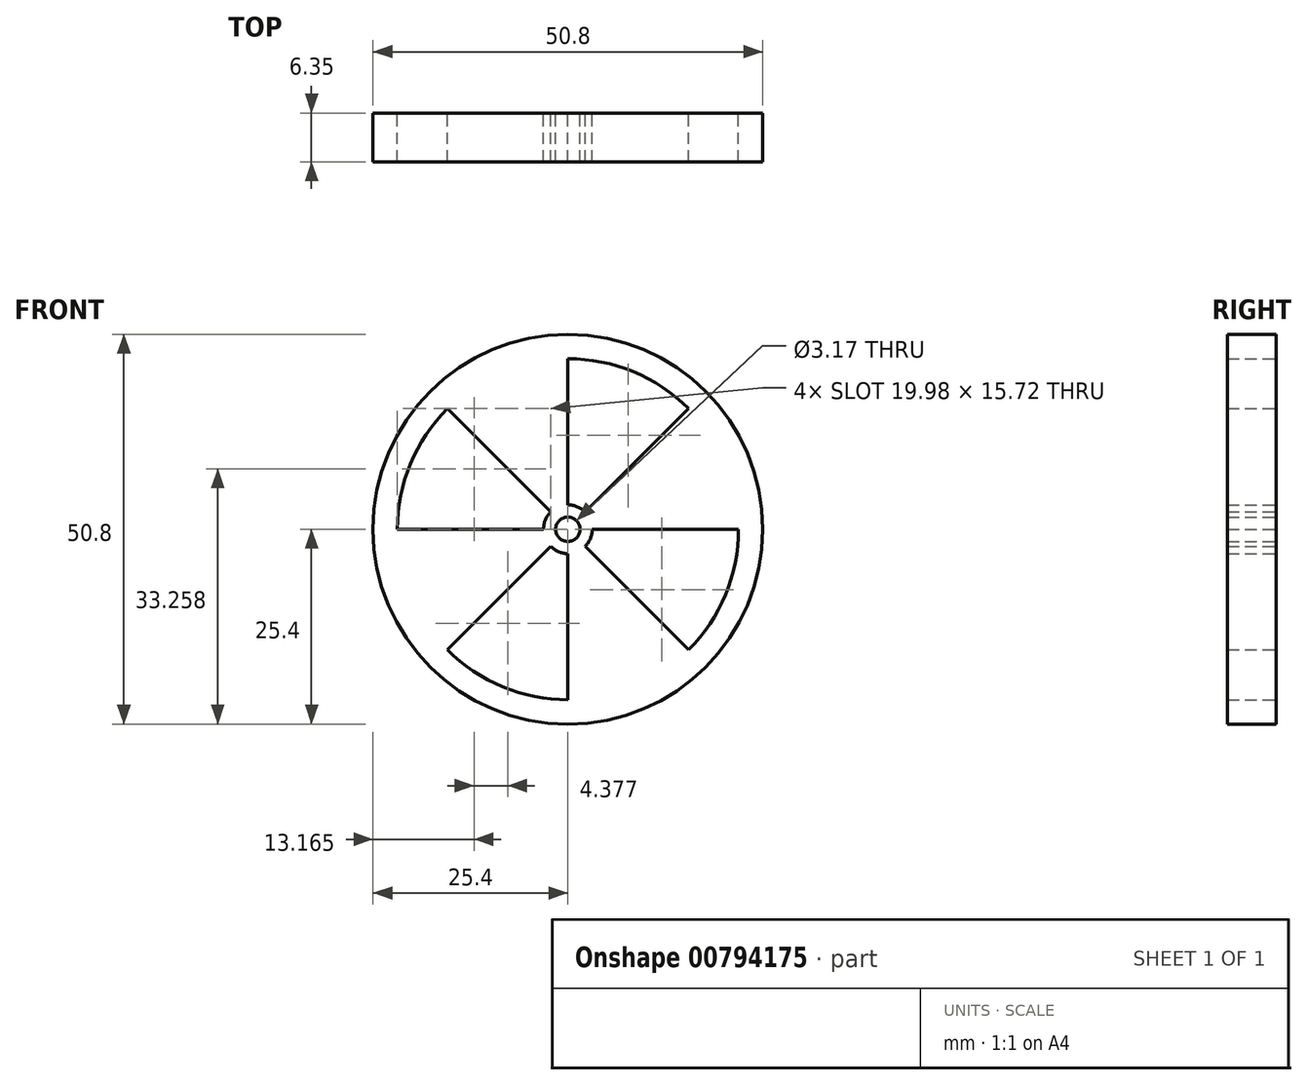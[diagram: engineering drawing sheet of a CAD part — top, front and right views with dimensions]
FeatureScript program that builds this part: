
annotation { "Feature Type Name" : "Feature", "Feature Type Description" : "" }
export const myFeature = defineFeature(function(context is Context, id is Id, definition is map)
    precondition{}
    {
        {
            var Q0;
            Q0=qCreatedBy(makeId("Front.planeOp"),FACE);
            var sketch = newSketch(context, id + "F0", { "sketchPlane" : qUnion([Q0])});
            skCircle(sketch, "E0", {"center": v(0, 0) * mm, "radius": 1.59 * mm});
            skCircle(sketch, "E1", {"center": v(0, 0) * mm, "radius": 3.18 * mm});
            skCircle(sketch, "E2", {"center": v(0, 0) * mm, "radius": 22.23 * mm});
            skCircle(sketch, "E3", {"center": v(0, 0) * mm, "radius": 25.4 * mm});
            skLineSegment(sketch, "E4", {"start": v(0, 3.18) * mm, "end": v(0, 22.23) * mm});
            skLineSegment(sketch, "E5.1.0", {"start": v(-3.18, 0) * mm, "end": v(-22.23, 0) * mm});
            skLineSegment(sketch, "E5.2.0", {"start": v(0, -3.18) * mm, "end": v(0, -22.23) * mm});
            skLineSegment(sketch, "E5.3.0", {"start": v(3.18, 0) * mm, "end": v(22.23, 0) * mm});
            skLineSegment(sketch, "E5.3.1", {"start": v(2.25, -2.25) * mm, "end": v(15.72, -15.72) * mm});
            skLineSegment(sketch, "E6.trimOffspring", {"start": v(-2.25, 2.25) * mm, "end": v(-15.72, 15.72) * mm});
            skLineSegment(sketch, "E7.trimOffspring", {"start": v(2.25, 2.25) * mm, "end": v(15.72, 15.72) * mm});
            skLineSegment(sketch, "E8.trimOffspring", {"start": v(-2.25, -2.25) * mm, "end": v(-15.72, -15.72) * mm});
            skSolve(sketch);
        }
        {
            var Q0;
            {var subQ0=sQuery(id+"F0.wireOp",EDGE,"E4");Q0=makeQuery(id+"F0.imprint","IMPRINT",FACE,{"disambiguationData":[TD([[makeQuery(id+"F0.imprint","IMPRINT",EDGE,{"derivedFrom":subQ0}),1.0]])]});}
            var Q1;
            {var subQ0=sQuery(id+"F0.wireOp",EDGE,"E5.3.0");Q1=makeQuery(id+"F0.imprint","IMPRINT",FACE,{"disambiguationData":[TD([[makeQuery(id+"F0.imprint","IMPRINT",EDGE,{"derivedFrom":subQ0}),1.0]])]});}
            var Q2;
            {var subQ0=sQuery(id+"F0.wireOp",EDGE,"E5.2.0");Q2=makeQuery(id+"F0.imprint","IMPRINT",FACE,{"disambiguationData":[TD([[makeQuery(id+"F0.imprint","IMPRINT",EDGE,{"derivedFrom":subQ0}),1.0]])]});}
            var Q3;
            {var subQ0=sQuery(id+"F0.wireOp",EDGE,"E5.1.0");Q3=makeQuery(id+"F0.imprint","IMPRINT",FACE,{"disambiguationData":[TD([[makeQuery(id+"F0.imprint","IMPRINT",EDGE,{"derivedFrom":subQ0}),1.0]])]});}
            var Q4;
            Q4=makeQuery(id+"F0.imprint","IMPRINT",FACE,{"disambiguationData":[TD([[makeQuery(id+"F0.imprint","IMPRINT",EDGE,{"derivedFrom":sQuery(id+"F0.wireOp",EDGE,"E3")}),1.0]])]});
            var Q5;
            Q5=makeQuery(id+"F0.imprint","IMPRINT",FACE,{"disambiguationData":[TD([[makeQuery(id+"F0.imprint","IMPRINT",EDGE,{"derivedFrom":sQuery(id+"F0.wireOp",EDGE,"E0")}),-1.0]])]});
            extrude(context, id + "F1", {"entities" : qUnion([Q0, Q1, Q2, Q3, Q4, Q5]), "depth" : 6.35 * mm, "offsetDistance" : 25.4 * mm});
        }
    });
